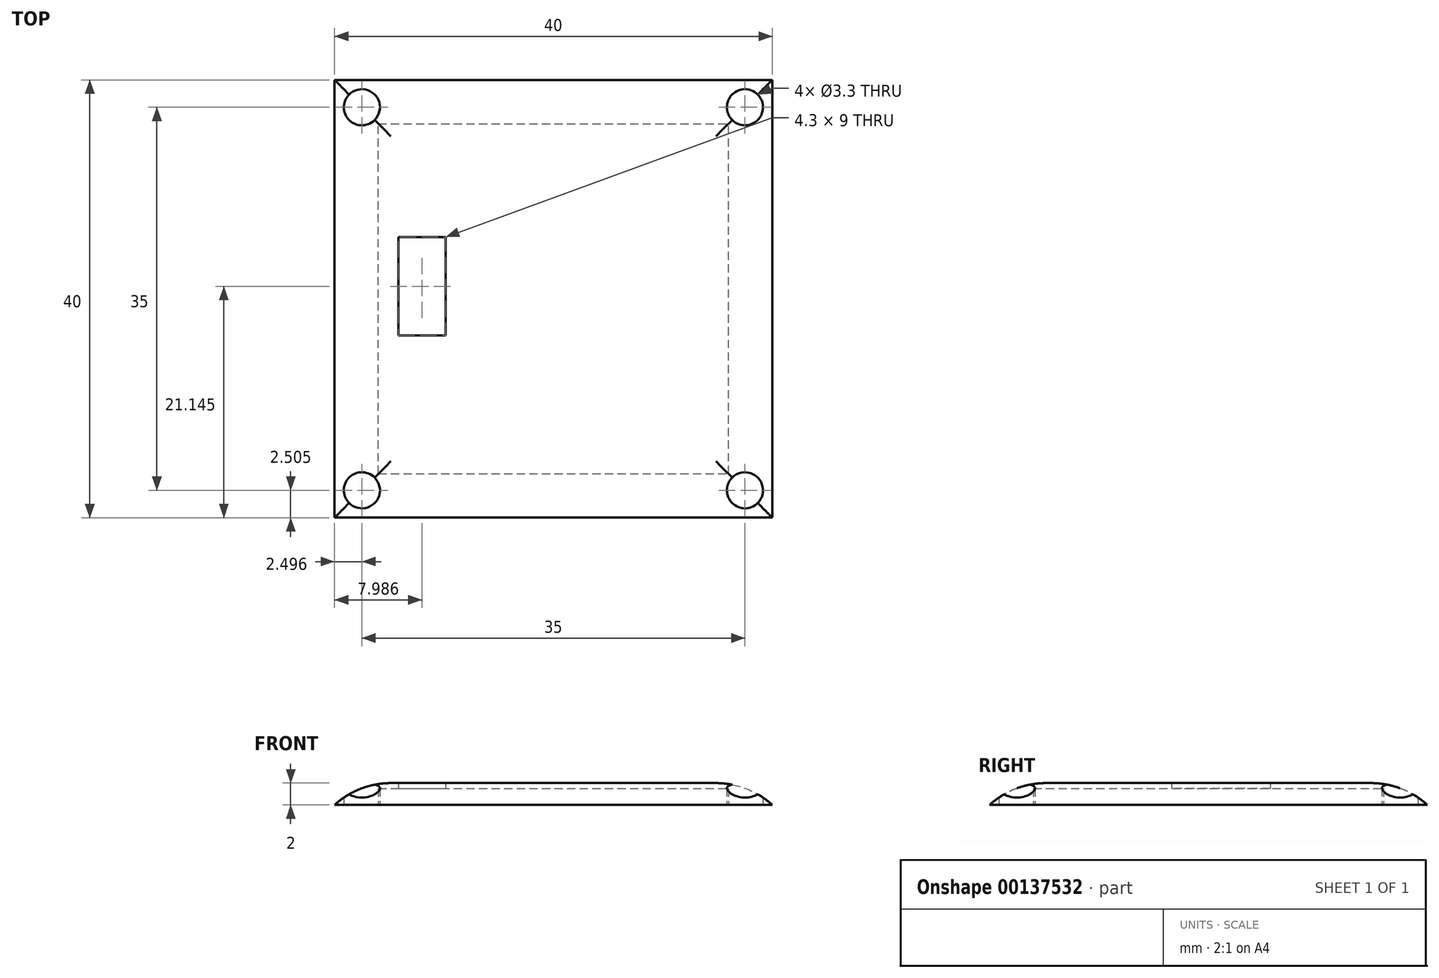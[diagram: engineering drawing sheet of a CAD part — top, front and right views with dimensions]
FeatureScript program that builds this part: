
annotation { "Feature Type Name" : "Feature", "Feature Type Description" : "" }
export const myFeature = defineFeature(function(context is Context, id is Id, definition is map)
    precondition{}
    {
        {
            var Q0;
            Q0=qCreatedBy(makeId("Top.planeOp"),FACE);
            var sketch = newSketch(context, id + "F0", { "sketchPlane" : qUnion([Q0])});
            skLineSegment(sketch, "E0.bottom", {"start": v(-19.08, 33.05) * mm, "end": v(20.92, 33.05) * mm});
            skLineSegment(sketch, "E0.top", {"start": v(-19.08, -6.95) * mm, "end": v(20.92, -6.95) * mm});
            skLineSegment(sketch, "E0.left", {"start": v(-19.08, 33.05) * mm, "end": v(-19.08, -6.95) * mm});
            skLineSegment(sketch, "E0.right", {"start": v(20.92, 33.05) * mm, "end": v(20.92, -6.95) * mm});
            skPoint(sketch, "E1", {"position": v(-16.58, 30.55) * mm});
            skPoint(sketch, "E2", {"position": v(-16.58, -4.45) * mm});
            skPoint(sketch, "E3", {"position": v(18.42, -4.45) * mm});
            skPoint(sketch, "E4", {"position": v(18.42, 30.55) * mm});
            skSolve(sketch);
        }
        {
            var Q0;
            Q0 = qSketchRegion(id + "F0", true);
            extrude(context, id + "F1", {"entities" : qUnion([Q0]), "depth" : 2 * mm});
        }
        {
            var Q0;
            Q0=makeQuery(id+"F1.opExtrude","CAP_FACE",FACE,{"disambiguationData":[OSD([sQuery(id+"F0.wireOp",EDGE,"E0.bottom"),sQuery(id+"F0.wireOp",EDGE,"E0.top"),sQuery(id+"F0.wireOp",EDGE,"E0.left"),sQuery(id+"F0.wireOp",EDGE,"E0.right")])],"isStart":false});
            fillet(context, id + "F2", {"entities" : qUnion([Q0]), "radius" : 7.62 * mm, "tangentPropagation" : true, "allowEdgeOverflow" : false});
        }
        {
            var Q0;
            Q0=sQuery(id+"F0.wireOp",VERTEX,"E2");
            var Q1;
            Q1=sQuery(id+"F0.wireOp",VERTEX,"E1");
            var Q2;
            Q2=sQuery(id+"F0.wireOp",VERTEX,"E4");
            var Q3;
            Q3=sQuery(id+"F0.wireOp",VERTEX,"E3");
            var Q4;
            Q4=makeQuery(id+"F1.opExtrude","SWEPT_BODY",BODY,{"disambiguationData":[OSD([sQuery(id+"F0.wireOp",EDGE,"E0.bottom"),sQuery(id+"F0.wireOp",EDGE,"E0.top"),sQuery(id+"F0.wireOp",EDGE,"E0.left"),sQuery(id+"F0.wireOp",EDGE,"E0.right")])]});
            hole(context, id + "F3", {"style" : HoleStyle.SIMPLE, "endStyle" : HoleEndStyle.THROUGH, "oppositeDirection" : true, "standardTappedOrClearance" : lookupTablePath({ "standard" : "ISO", "fit" : "Normal", "size" : "M3", "type" : "Clearance" }), "standardBlindInLast" : lookupTablePath({ "fit" : "Standard", "standard" : "ISO", "size" : "M3", "type" : "Clearance" }), "holeDiameter" : 3.3 * mm, "locations" : qUnion([Q0, Q1, Q2, Q3]), "scope" : qUnion([Q4]), "isTappedThrough" : true});
        }
        {
            var Q0;
            Q0=qCreatedBy(makeId("Top.planeOp"),FACE);
            var sketch = newSketch(context, id + "F4", { "sketchPlane" : qUnion([Q0])});
            skLineSegment(sketch, "E5.bottom", {"start": v(-13.24, 18.7) * mm, "end": v(-8.94, 18.7) * mm});
            skLineSegment(sketch, "E5.top", {"start": v(-13.24, 9.7) * mm, "end": v(-8.94, 9.7) * mm});
            skLineSegment(sketch, "E5.left", {"start": v(-13.24, 18.7) * mm, "end": v(-13.24, 9.7) * mm});
            skLineSegment(sketch, "E5.right", {"start": v(-8.94, 18.7) * mm, "end": v(-8.94, 9.7) * mm});
            skSolve(sketch);
        }
        {
            var Q0;
            Q0 = qSketchRegion(id + "F4", true);
            extrude(context, id + "F5", {"entities" : qUnion([Q0]), "operationType" : NewBodyOperationType.REMOVE, "depth" : 25 * mm});
        }
        {
            var Q0;
            Q0=qCreatedBy(makeId("Top.planeOp"),FACE);
            var sketch = newSketch(context, id + "F6", { "sketchPlane" : qUnion([Q0])});
            skLineSegment(sketch, "E6.bottom", {"start": v(-15.08, -2.95) * mm, "end": v(16.92, -2.95) * mm});
            skLineSegment(sketch, "E6.top", {"start": v(-15.08, 29.05) * mm, "end": v(16.92, 29.05) * mm});
            skLineSegment(sketch, "E6.left", {"start": v(-15.08, -2.95) * mm, "end": v(-15.08, 29.05) * mm});
            skLineSegment(sketch, "E6.right", {"start": v(16.92, -2.95) * mm, "end": v(16.92, 29.05) * mm});
            skSolve(sketch);
        }
        {
            var Q0;
            Q0 = qSketchRegion(id + "F6", true);
            extrude(context, id + "F7", {"entities" : qUnion([Q0]), "operationType" : NewBodyOperationType.REMOVE, "depth" : 1.5 * mm});
        }
    });
